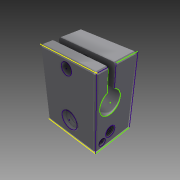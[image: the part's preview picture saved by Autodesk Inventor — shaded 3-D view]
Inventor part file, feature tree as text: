
AUTODESK INVENTOR PART (.ipt)
format: ipt  version: 2015 (Build 190159000, 159)  size: 397,824 bytes
history: native  units: mm
features: sketch x4, hole x4, other x3, extrude x2, chamfer x1
ambient origin geometry x8: Origin, YZ Plane, XZ Plane, XY Plane, X Axis, Y Axis, Z Axis, Center Point
bodies: Body1 (feature_tree)
feature tree (14):
  other  "Твердое тело1"
  extrude  "Выдавливание1"  Depth=3.025mm
  sketch  "Эскиз2"
  hole  "Отверстие1"  [1 undecoded]
  hole  "Отверстие3"  [1 undecoded]
  hole  "Отверстие4"  [1 undecoded]
  sketch  "Эскиз3"
  hole  "Отверстие2"  [1 undecoded]
  extrude  "Выдавливание4"  Depth=4.0mm
  chamfer  "Фаска1"  Distance=16.0mm
  other  "РабПлоскость2"
  other  "Пружина2"
  sketch  "Эскиз1"
  sketch  "Эскиз5"
note: 4 required parameter values undecoded (feature->parameter linkage not recoverable at this tier; creation-order binding heuristic only, values carry confidence <= 0.55)
